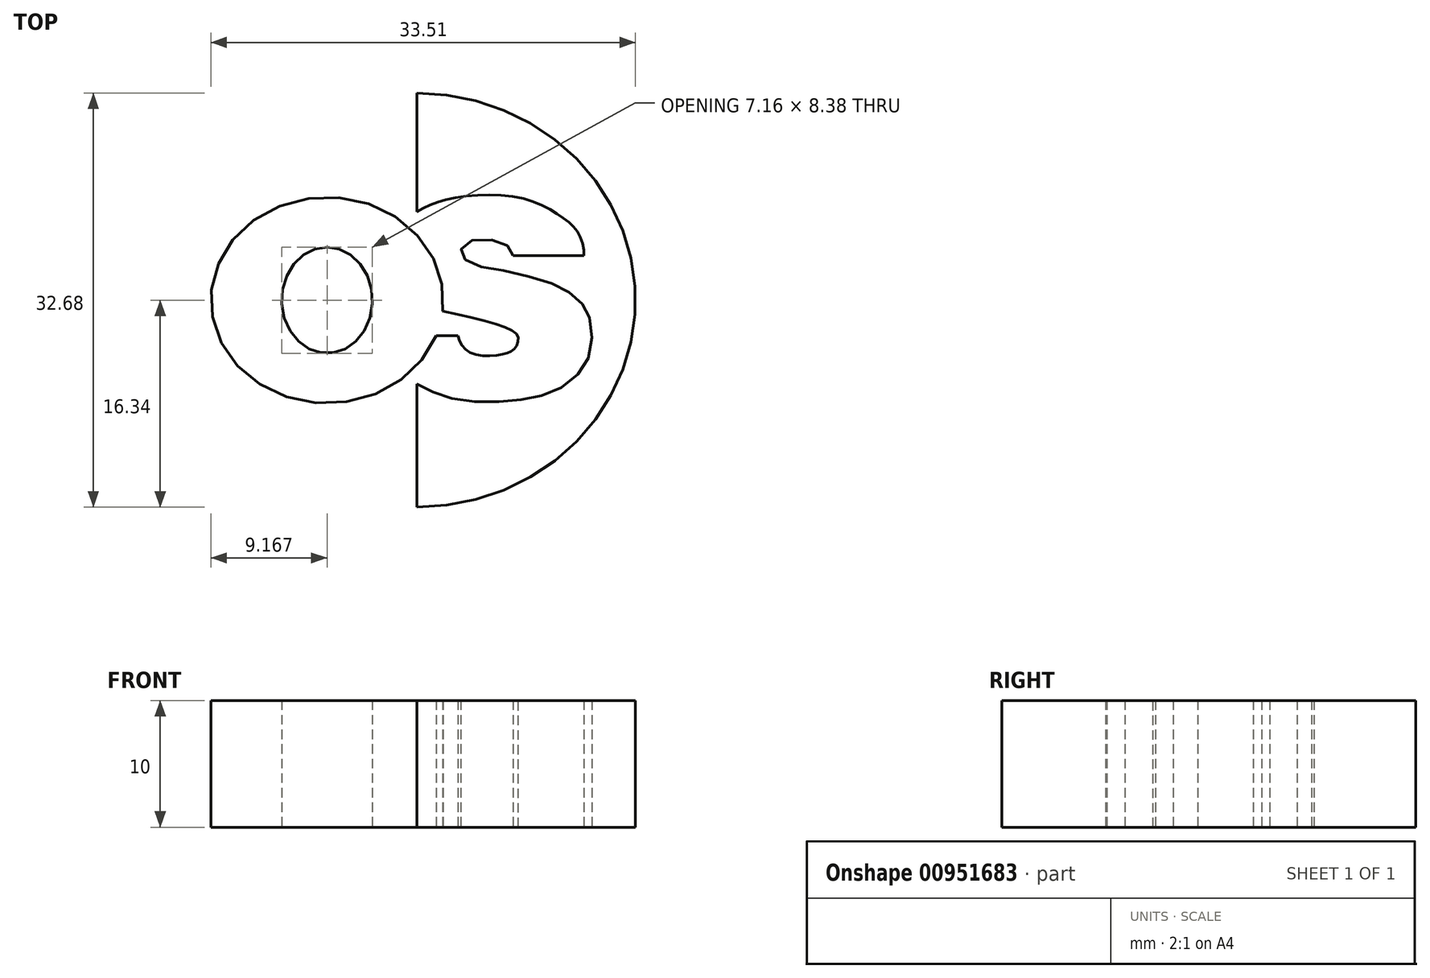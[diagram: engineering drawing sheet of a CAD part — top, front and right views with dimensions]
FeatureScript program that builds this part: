
annotation { "Feature Type Name" : "Feature", "Feature Type Description" : "" }
export const myFeature = defineFeature(function(context is Context, id is Id, definition is map)
    precondition{}
    {
        {
            var Q0;
            Q0=qCreatedBy(makeId("Top.planeOp"),FACE);
            var sketch = newSketch(context, id + "F0", { "sketchPlane" : qUnion([Q0])});
            skEllipse(sketch, "E0", {"center": v(0, 0) * mm, "majorRadius": 18.42 * mm, "minorRadius": 19.28 * mm, "majorAxis": v(0, 1)});
            skEllipticalArc(sketch, "E1", {});
            skEllipse(sketch, "E2", {"center": v(-7.08, 0) * mm, "majorRadius": 4.2 * mm, "minorRadius": 3.58 * mm, "majorAxis": v(0, 1)});
            skEllipticalArc(sketch, "E3", {});
            skLineSegment(sketch, "E4", {"start": v(0, 16.34) * mm, "end": v(0, 6.99) * mm});
            skLineSegment(sketch, "E5", {"start": v(0, -6.61) * mm, "end": v(0, -16.34) * mm});
            skFitSpline(sketch, "E6", {"points": [v(0, 6.99) * mm, v(2.69, 8.01) * mm, v(8.28, 8.04) * mm, v(11.51, 6.51) * mm, v(12.8, 5.2) * mm, v(13.2, 3.52) * mm], "startDerivative": vector(11.6, 7.03) * mm, "endDerivative": vector(-0.27, -9.65) * mm});
            skLineSegment(sketch, "E7", {"start": v(13.2, 3.52) * mm, "end": v(7.61, 3.52) * mm});
            skFitSpline(sketch, "E8", {"points": [v(7.61, 3.52) * mm, v(7.34, 4.12) * mm, v(6.38, 4.64) * mm, v(4.4, 4.73) * mm, v(3.55, 4.12) * mm, v(3.55, 3.52) * mm, v(4.5, 2.8) * mm, v(6.82, 2.34) * mm, v(10.06, 1.51) * mm, v(11.98, 0.66) * mm, v(13.13, -0.38) * mm, v(13.68, -1.53) * mm, v(13.74, -3.81) * mm, v(13, -5.54) * mm, v(11.26, -6.97) * mm, v(9.1, -7.71) * mm, v(6.68, -8.01) * mm, v(3.74, -7.93) * mm, v(1.52, -7.35) * mm, v(0, -6.61) * mm], "startDerivative": vector(-5.92, 19.87) * mm, "endDerivative": vector(-28.15, 15.2) * mm});
            skFitSpline(sketch, "E9", {"points": [v(2.03, -0.88) * mm, v(7.2, -2.24) * mm, v(7.99, -2.84) * mm, v(7.94, -3.44) * mm, v(7.65, -3.89) * mm, v(7.16, -4.16) * mm, v(6.1, -4.37) * mm, v(4.53, -4.26) * mm, v(3.63, -3.67) * mm, v(3.24, -2.8) * mm], "startDerivative": vector(27.73, -5.84) * mm, "endDerivative": vector(-3.04, 9.34) * mm});
            skLineSegment(sketch, "E10", {"start": v(3.24, -2.8) * mm, "end": v(1.52, -2.8) * mm});
            const initialGuessF0  = {"E1": [0, 0, 0, 1, 0.016336938366293907, 0.01726117617026608, 3.141592653589793, 6.283185307179586], "E3": [-0.007082561030983925, 0, 0, 1, 0.008139732798417341, 0.009165805267224644, 4.6041913365112315, 4.36023600412348]};
            skSetInitialGuess(sketch, initialGuessF0);
            skSolve(sketch);
        }
        {
            var Q0;
            Q0=makeQuery(id+"F0.imprint","IMPRINT",FACE,{"disambiguationData":[TD([[makeQuery(id+"F0.imprint","IMPRINT",EDGE,{"derivedFrom":sQuery(id+"F0.wireOp",EDGE,"E2")}),-1.0]])]});
            var Q1;
            Q1=makeQuery(id+"F0.imprint","IMPRINT",FACE,{"disambiguationData":[TD([[makeQuery(id+"F0.imprint","IMPRINT",EDGE,{"derivedFrom":sQuery(id+"F0.wireOp",EDGE,"E1")}),1.0]])]});
            extrude(context, id + "F1", {"entities" : qUnion([Q0, Q1]), "depth" : 10 * mm, "offsetDistance" : 25 * mm});
        }
    });
